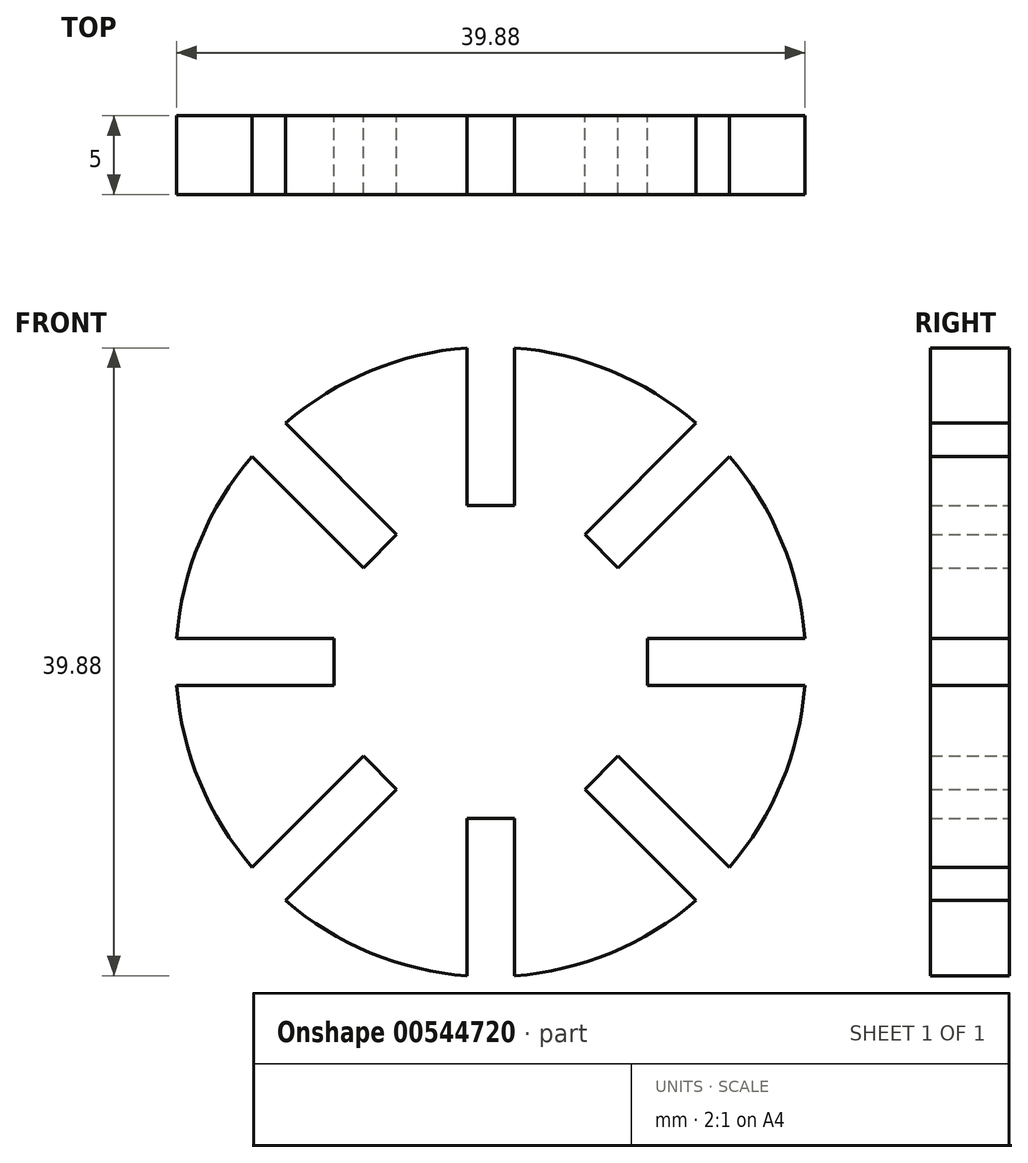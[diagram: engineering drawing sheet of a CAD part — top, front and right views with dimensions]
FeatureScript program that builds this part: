
annotation { "Feature Type Name" : "Feature", "Feature Type Description" : "" }
export const myFeature = defineFeature(function(context is Context, id is Id, definition is map)
    precondition{}
    {
        {
            var Q0;
            Q0=qCreatedBy(makeId("Front.planeOp"),FACE);
            var sketch = newSketch(context, id + "F0", { "sketchPlane" : qUnion([Q0])});
            skPoint(sketch, "E0", {"position": v(-1.5, 19.94) * mm});
            skPoint(sketch, "E1", {"position": v(1.5, 19.94) * mm});
            skLineSegment(sketch, "E2", {"start": v(-1.5, 19.94) * mm, "end": v(-1.5, 9.94) * mm});
            skLineSegment(sketch, "E3", {"start": v(1.5, 19.94) * mm, "end": v(1.5, 9.94) * mm});
            skLineSegment(sketch, "E4", {"start": v(-1.5, 9.94) * mm, "end": v(1.5, 9.94) * mm});
            skLineSegment(sketch, "E5.1.0", {"start": v(-15.16, 13.04) * mm, "end": v(-8.1, 5.97) * mm});
            skPoint(sketch, "E5.1.1", {"position": v(-13.04, 15.16) * mm});
            skPoint(sketch, "E5.1.3", {"position": v(-15.16, 13.04) * mm});
            skLineSegment(sketch, "E5.1.4", {"start": v(-13.04, 15.16) * mm, "end": v(-5.97, 8.1) * mm});
            skLineSegment(sketch, "E5.1.5", {"start": v(-8.1, 5.97) * mm, "end": v(-5.97, 8.1) * mm});
            skLineSegment(sketch, "E5.2.0", {"start": v(-19.94, -1.5) * mm, "end": v(-9.94, -1.5) * mm});
            skPoint(sketch, "E5.2.1", {"position": v(-19.94, 1.5) * mm});
            skArc(sketch, "E5.2.2", {"start": v(-19.94, -1.5) * mm, "mid": v(-18.48, -7.65) * mm, "end": v(-15.16, -13.04) * mm});
            skPoint(sketch, "E5.2.3", {"position": v(-19.94, -1.5) * mm});
            skLineSegment(sketch, "E5.2.4", {"start": v(-19.94, 1.5) * mm, "end": v(-9.94, 1.5) * mm});
            skLineSegment(sketch, "E5.2.5", {"start": v(-9.94, -1.5) * mm, "end": v(-9.94, 1.5) * mm});
            skLineSegment(sketch, "E5.3.0", {"start": v(-13.04, -15.16) * mm, "end": v(-5.97, -8.1) * mm});
            skPoint(sketch, "E5.3.1", {"position": v(-15.16, -13.04) * mm});
            skPoint(sketch, "E5.3.3", {"position": v(-13.04, -15.16) * mm});
            skLineSegment(sketch, "E5.3.4", {"start": v(-15.16, -13.04) * mm, "end": v(-8.1, -5.97) * mm});
            skLineSegment(sketch, "E5.3.5", {"start": v(-5.97, -8.1) * mm, "end": v(-8.1, -5.97) * mm});
            skLineSegment(sketch, "E5.4.0", {"start": v(1.5, -19.94) * mm, "end": v(1.5, -9.94) * mm});
            skPoint(sketch, "E5.4.1", {"position": v(-1.5, -19.94) * mm});
            skPoint(sketch, "E5.4.3", {"position": v(1.5, -19.94) * mm});
            skLineSegment(sketch, "E5.4.4", {"start": v(-1.5, -19.94) * mm, "end": v(-1.5, -9.94) * mm});
            skLineSegment(sketch, "E5.4.5", {"start": v(1.5, -9.94) * mm, "end": v(-1.5, -9.94) * mm});
            skLineSegment(sketch, "E5.5.0", {"start": v(15.16, -13.04) * mm, "end": v(8.1, -5.97) * mm});
            skPoint(sketch, "E5.5.1", {"position": v(13.04, -15.16) * mm});
            skArc(sketch, "E5.5.2", {"start": v(15.16, -13.04) * mm, "mid": v(18.48, -7.65) * mm, "end": v(19.94, -1.5) * mm});
            skPoint(sketch, "E5.5.3", {"position": v(15.16, -13.04) * mm});
            skLineSegment(sketch, "E5.5.4", {"start": v(13.04, -15.16) * mm, "end": v(5.97, -8.1) * mm});
            skLineSegment(sketch, "E5.5.5", {"start": v(8.1, -5.97) * mm, "end": v(5.97, -8.1) * mm});
            skLineSegment(sketch, "E5.6.0", {"start": v(19.94, 1.5) * mm, "end": v(9.94, 1.5) * mm});
            skPoint(sketch, "E5.6.1", {"position": v(19.94, -1.5) * mm});
            skPoint(sketch, "E5.6.3", {"position": v(19.94, 1.5) * mm});
            skLineSegment(sketch, "E5.6.4", {"start": v(19.94, -1.5) * mm, "end": v(9.94, -1.5) * mm});
            skLineSegment(sketch, "E5.6.5", {"start": v(9.94, 1.5) * mm, "end": v(9.94, -1.5) * mm});
            skLineSegment(sketch, "E5.7.0", {"start": v(13.04, 15.16) * mm, "end": v(5.97, 8.1) * mm});
            skPoint(sketch, "E5.7.1", {"position": v(15.16, 13.04) * mm});
            skPoint(sketch, "E5.7.3", {"position": v(13.04, 15.16) * mm});
            skLineSegment(sketch, "E5.7.4", {"start": v(15.16, 13.04) * mm, "end": v(8.1, 5.97) * mm});
            skLineSegment(sketch, "E5.7.5", {"start": v(5.97, 8.1) * mm, "end": v(8.1, 5.97) * mm});
            skPoint(sketch, "E5.center", {"position": v(0, 0) * mm});
            skArc(sketch, "E6.trimOffspring", {"start": v(-1.5, 19.94) * mm, "mid": v(-7.65, 18.48) * mm, "end": v(-13.04, 15.16) * mm});
            skArc(sketch, "E7.trimOffspring", {"start": v(-15.16, 13.04) * mm, "mid": v(-18.48, 7.65) * mm, "end": v(-19.94, 1.5) * mm});
            skArc(sketch, "E8.trimOffspring", {"start": v(13.04, 15.16) * mm, "mid": v(7.65, 18.48) * mm, "end": v(1.5, 19.94) * mm});
            skArc(sketch, "E9.trimOffspring", {"start": v(19.94, 1.5) * mm, "mid": v(18.48, 7.65) * mm, "end": v(15.16, 13.04) * mm});
            skArc(sketch, "E10.trimOffspring", {"start": v(1.5, -19.94) * mm, "mid": v(7.65, -18.48) * mm, "end": v(13.04, -15.16) * mm});
            skArc(sketch, "E11.trimOffspring", {"start": v(-13.04, -15.16) * mm, "mid": v(-7.65, -18.48) * mm, "end": v(-1.5, -19.94) * mm});
            skSolve(sketch);
        }
        {
            var Q0;
            Q0=qSketchRegion(id+"F0",true);
            extrude(context, id + "F1", {"entities" : qUnion([Q0]), "depth" : 5 * mm, "offsetDistance" : 25 * mm});
        }
    });
